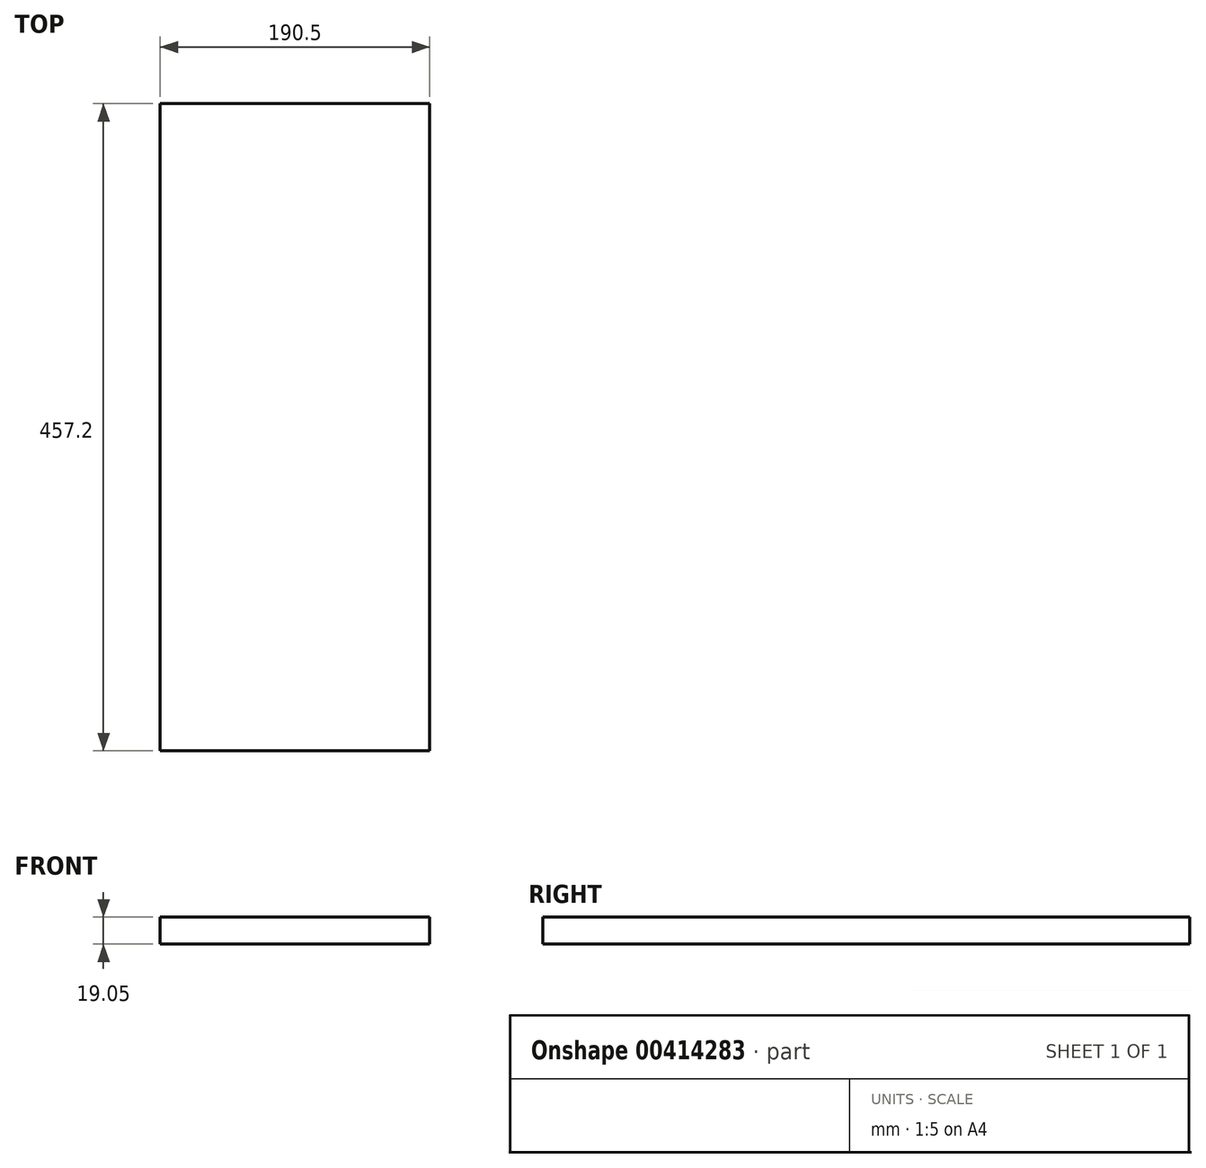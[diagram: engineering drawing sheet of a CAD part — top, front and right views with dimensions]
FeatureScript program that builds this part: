
annotation { "Feature Type Name" : "Feature", "Feature Type Description" : "" }
export const myFeature = defineFeature(function(context is Context, id is Id, definition is map)
    precondition{}
    {
        {
            var Q0;
            Q0=qCreatedBy(makeId("Front.planeOp"),FACE);
            var sketch = newSketch(context, id + "F0", { "sketchPlane" : qUnion([Q0])});
            skLineSegment(sketch, "E0.bottom", {"start": v(0, 0) * mm, "end": v(-190.5, 0) * mm});
            skLineSegment(sketch, "E0.top", {"start": v(0, 19.05) * mm, "end": v(-190.5, 19.05) * mm});
            skLineSegment(sketch, "E0.left", {"start": v(0, 0) * mm, "end": v(0, 19.05) * mm});
            skLineSegment(sketch, "E0.right", {"start": v(-190.5, 0) * mm, "end": v(-190.5, 19.05) * mm});
            skSolve(sketch);
        }
        {
            var Q0;
            Q0 = qSketchRegion(id + "F0", true);
            extrude(context, id + "F1", {"entities" : qUnion([Q0]), "depth" : 457.2 * mm});
        }
    });
